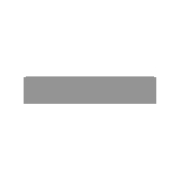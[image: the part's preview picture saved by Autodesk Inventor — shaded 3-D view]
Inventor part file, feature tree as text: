
AUTODESK INVENTOR PART (.ipt)
format: ipt  version: 2019 (Build 230136000, 136)  size: 113,152 bytes
history: native  units: mm
features: other x10, sketch x3, extrude x1
ambient origin geometry x8: Origin, YZ Plane, XZ Plane, XY Plane, X Axis, Y Axis, Z Axis, Center Point
bodies: Body1 (feature_tree)
feature tree (14):
  other  "Контрольная длина"
  other  "Генератор рам"
  other  "Твердое тело1"
  other  "Начальная плоскость"
  other  "Конечная плоскость"
  extrude  "Тело"  [1 undecoded]
  other  "РабПлоскость6"
  other  "Разделение1"
  other  "РабПлоскость7"
  other  "Разделение2"
  sketch  "Эскиз"
  sketch  "Эскиз6"
  other  "РабПлоскость5"
  sketch  "Эскиз7"
note: 1 required parameter value undecoded (feature->parameter linkage not recoverable at this tier; creation-order binding heuristic only, values carry confidence <= 0.55)
